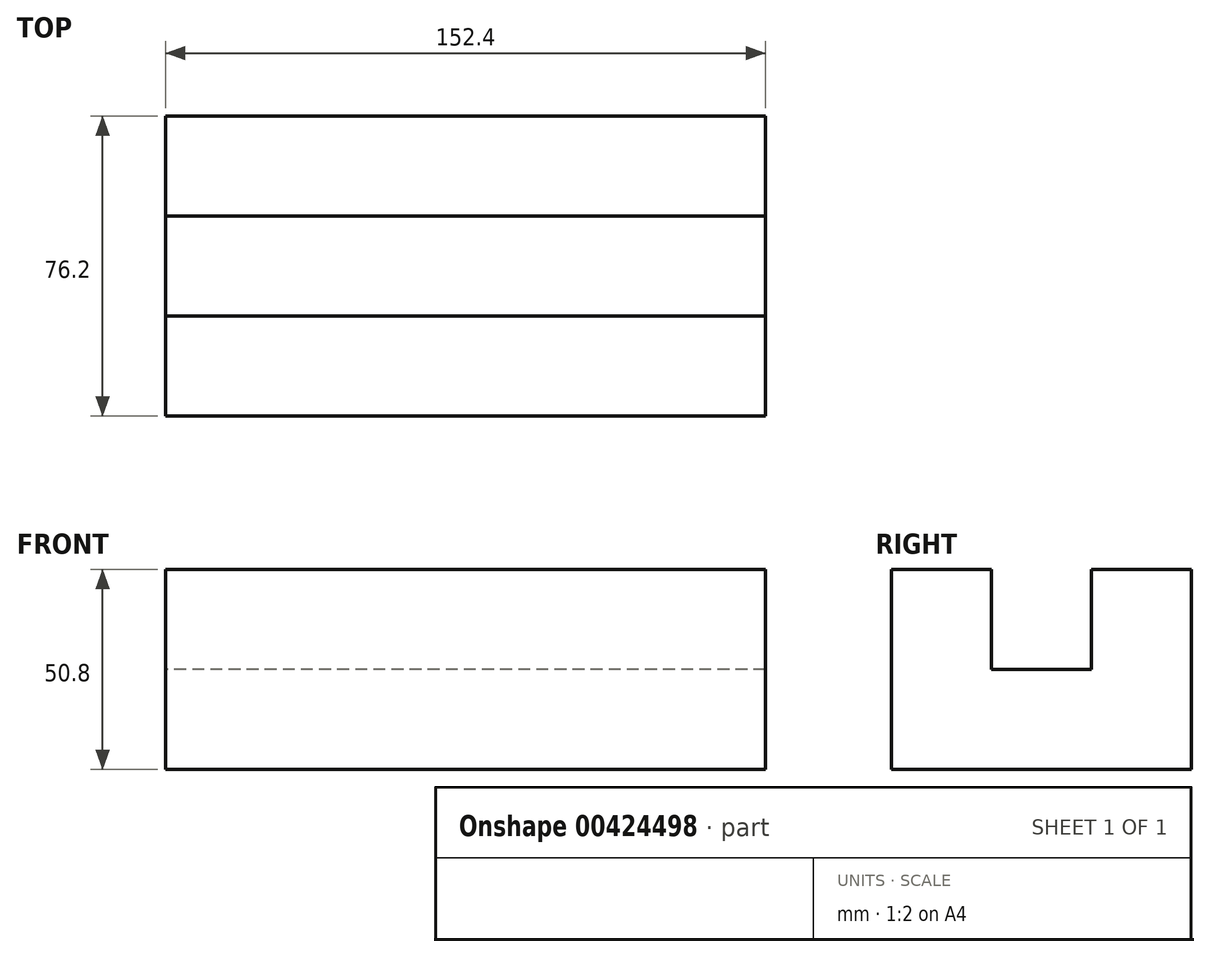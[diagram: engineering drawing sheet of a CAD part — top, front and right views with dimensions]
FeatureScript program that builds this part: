
annotation { "Feature Type Name" : "Feature", "Feature Type Description" : "" }
export const myFeature = defineFeature(function(context is Context, id is Id, definition is map)
    precondition{}
    {
        {
            var Q0;
            Q0=qCreatedBy(makeId("Right.planeOp"),FACE);
            var sketch = newSketch(context, id + "F0", { "sketchPlane" : qUnion([Q0])});
            skLineSegment(sketch, "E0", {"start": v(0, 0) * mm, "end": v(76.2, 0) * mm});
            skLineSegment(sketch, "E1", {"start": v(0, 0) * mm, "end": v(0, 50.8) * mm});
            skLineSegment(sketch, "E2", {"start": v(0, 50.8) * mm, "end": v(25.4, 50.8) * mm});
            skLineSegment(sketch, "E3", {"start": v(25.4, 50.8) * mm, "end": v(25.4, 25.4) * mm});
            skLineSegment(sketch, "E4", {"start": v(25.4, 25.4) * mm, "end": v(50.8, 25.4) * mm});
            skLineSegment(sketch, "E5", {"start": v(50.8, 25.4) * mm, "end": v(50.8, 50.8) * mm});
            skLineSegment(sketch, "E6", {"start": v(50.8, 50.8) * mm, "end": v(76.2, 50.8) * mm});
            skLineSegment(sketch, "E7", {"start": v(76.2, 50.8) * mm, "end": v(76.2, 0) * mm});
            skSolve(sketch);
        }
        {
            var Q0;
            Q0=makeQuery(id+"F0.imprint","IMPRINT",FACE,{"disambiguationData":[TD([[makeQuery(id+"F0.imprint","IMPRINT",EDGE,{"derivedFrom":sQuery(id+"F0.wireOp",EDGE,"E0")}),1.0]])]});
            extrude(context, id + "F1", {"entities" : qUnion([Q0]), "depth" : 152.4 * mm});
        }
    });
